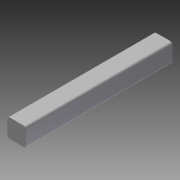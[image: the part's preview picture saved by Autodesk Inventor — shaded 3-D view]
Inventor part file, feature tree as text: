
AUTODESK INVENTOR PART (.ipt)
format: ipt  version: 2014 SP1 (Build 180222100, 222)  size: 84,480 bytes
history: native  units: in
note: dims shown in document units (in); Inventor stores cm internally (conversion verified against a paired STEP export)
features: plane x2, extrude x1, fillet x1, other x1, sketch x1
ambient origin geometry x8: Origin, YZ Plane, XZ Plane, XY Plane, X Axis, Y Axis, Z Axis, Center Point
bodies: Solid1 (feature_tree)
feature tree (6):
  extrude  "Extrusion1"  Depth=0.127in
  fillet  "Fillet1"  Radius=1.0in
  other  "Work Axis1"
  sketch  "Sketch1"  dims[d0=0.127in d1=0.127in d2=1.0in d3=0.0in d4=0.015in]
  plane  "Work Plane1"
  plane  "Work Plane2"
